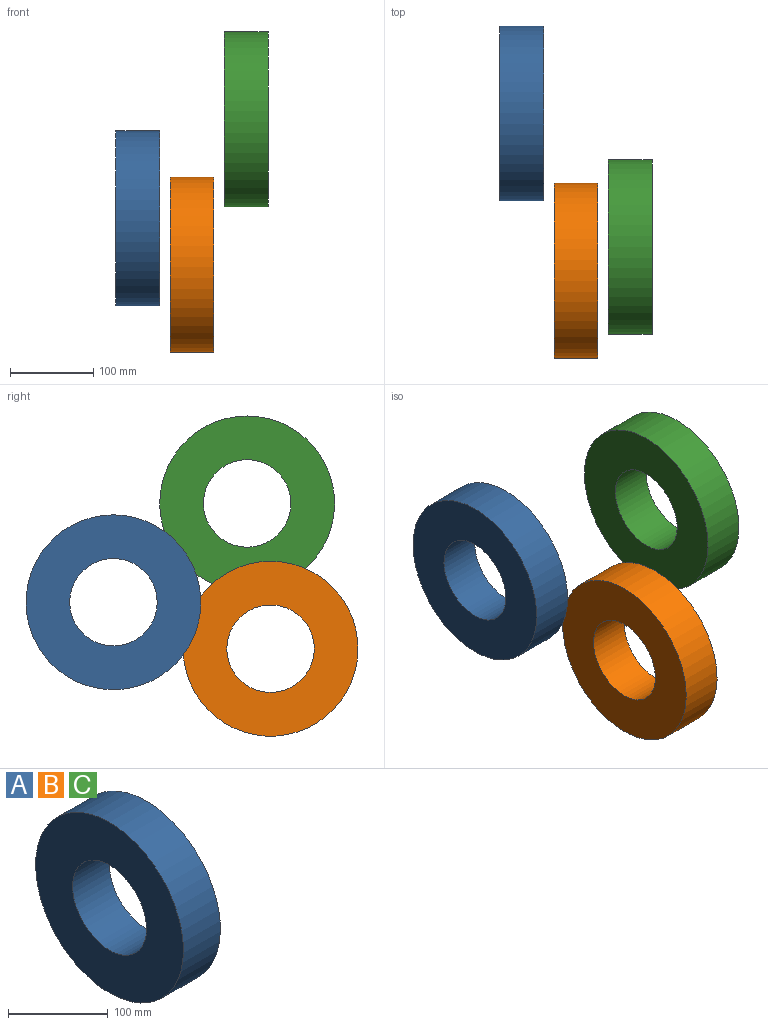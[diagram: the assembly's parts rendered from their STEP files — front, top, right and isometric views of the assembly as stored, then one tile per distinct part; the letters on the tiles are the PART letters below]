
ASSEMBLY  parts=3 mates=2
PART A: 4 faces, bbox 52.4x209.8x209.8 mm
  f0: plane 209.77x209.77mm, normal (-1,0,0), area 25920.5mm2, adj f1,f3
  f1: cylinder r=104.89mm len=209.77mm, axis (-1,0,0), area 34560.6mm2, adj f0,f2
  f2: plane 209.77x209.77mm, normal (1,0,0), area 25920.5mm2, adj f1,f3
  f3: cylinder r=52.44mm len=104.89mm, axis (-1,0,0), area 17280.3mm2, adj f0,f2
PART B: same geometry as A
PART C: same geometry as A
PLACE A t=(-12.46,0,0)mm
PLACE B t=(52.68,-188.53,-55.76)mm
PLACE C t=(117.82,-160.46,118.62)mm
MATE planar B.f1 <-> A.f1  axis (-1,0,0) through (105.12,-188.53,-55.76)mm
MATE planar C.f1 <-> B.f1  axis (-1,0,0) through (170.26,-160.46,118.62)mm
